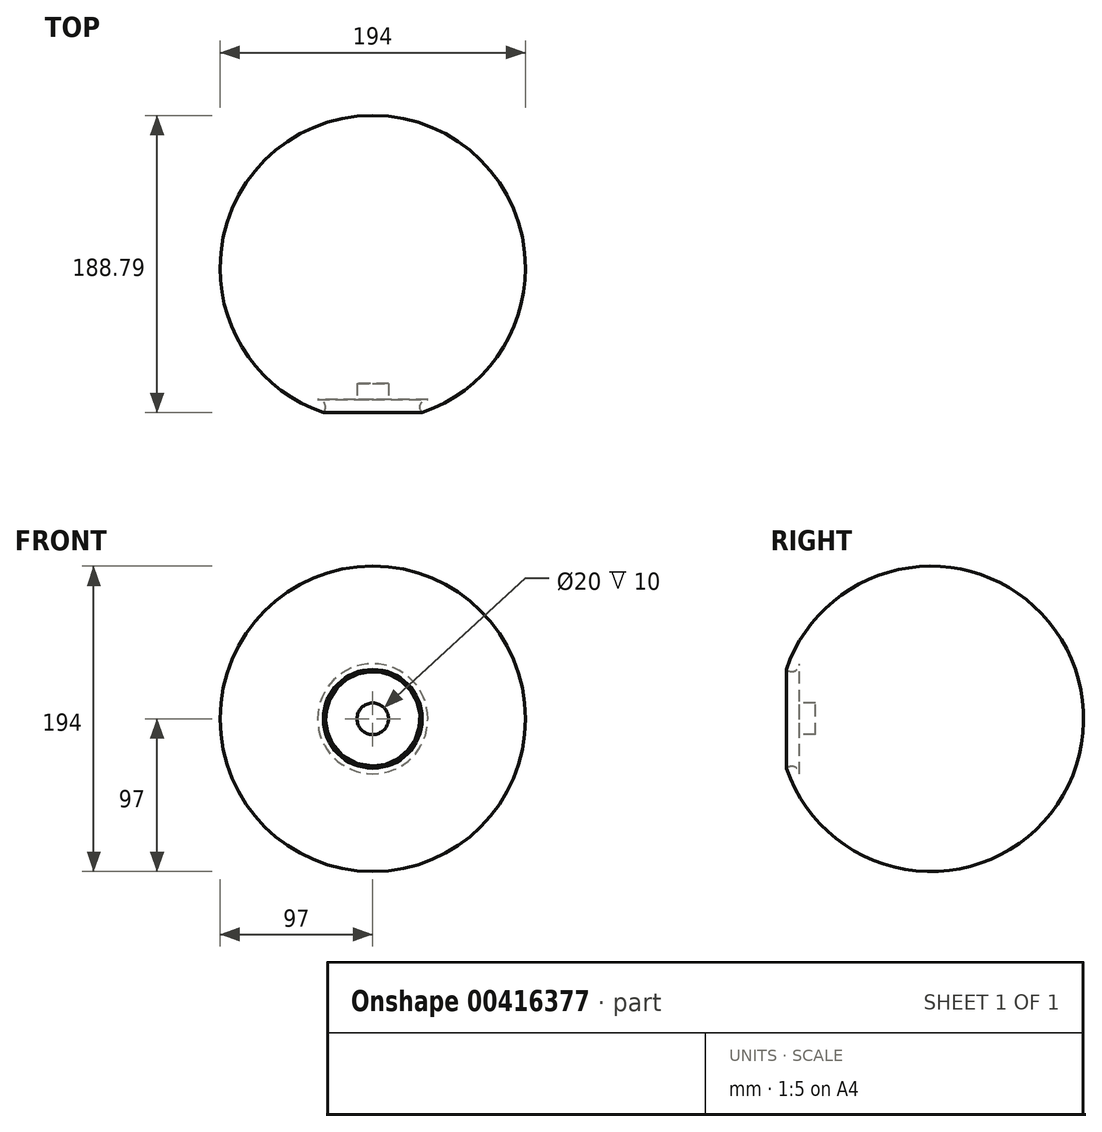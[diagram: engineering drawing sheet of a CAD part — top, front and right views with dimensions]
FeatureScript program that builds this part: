
annotation { "Feature Type Name" : "Feature", "Feature Type Description" : "" }
export const myFeature = defineFeature(function(context is Context, id is Id, definition is map)
    precondition{}
    {
        {
            var Q0;
            Q0=qCreatedBy(makeId("Front.planeOp"),FACE);
            var sketch = newSketch(context, id + "F0", { "sketchPlane" : qUnion([Q0])});
            skCircle(sketch, "E0", {"center": v(0, 0) * mm, "radius": 97 * mm});
            skCircle(sketch, "E1", {"center": v(-0.22, 0.55) * mm, "radius": 40 * mm});
            skLineSegment(sketch, "E2", {"start": v(0, 0) * mm, "end": v(97, 0) * mm});
            skLineSegment(sketch, "E3", {"start": v(0, 0) * mm, "end": v(-97, 0) * mm});
            skCircle(sketch, "E4", {"center": v(0, 0) * mm, "radius": 92 * mm});
            skSolve(sketch);
        }
        {
            var Q0;
            Q0=qCreatedBy(makeId("Right.planeOp"),FACE);
            var sketch = newSketch(context, id + "F1", { "sketchPlane" : qUnion([Q0])});
            skCircle(sketch, "E5", {"center": v(0, 0) * mm, "radius": 97 * mm});
            skLineSegment(sketch, "E6", {"start": v(0, 0) * mm, "end": v(-97, 0) * mm});
            skLineSegment(sketch, "E7", {"start": v(-88.37, 0) * mm, "end": v(-88.37, 40) * mm});
            skLineSegment(sketch, "E8", {"start": v(-88.37, 40) * mm, "end": v(-88.37, 35) * mm});
            skCircle(sketch, "E9", {"center": v(-88.37, 35) * mm, "radius": 5 * mm});
            skLineSegment(sketch, "E10", {"start": v(-83.37, 35) * mm, "end": v(-83.37, 10) * mm});
            skLineSegment(sketch, "E11", {"start": v(-83.37, 10) * mm, "end": v(-83.37, 0) * mm});
            skLineSegment(sketch, "E12", {"start": v(-83.37, 10) * mm, "end": v(-73.37, 10) * mm});
            skLineSegment(sketch, "E13", {"start": v(-73.37, 10) * mm, "end": v(-73.37, 0) * mm});
            skSolve(sketch);
        }
        {
            var Q0;
            {var subQ0=sQuery(id+"F0.wireOp",EDGE,"E2");var subQ1=sQuery(id+"F0.wireOp",EDGE,"E0");var subQ2=makeQuery(id+"F0.imprint","INTERSECT",VERTEX,{"derivedFrom":[subQ1,subQ0]});Q0=makeQuery(id+"F0.imprint","IMPRINT",FACE,{"disambiguationData":[TD([[makeQuery(id+"F0.imprint","IMPRINT",EDGE,{"disambiguationData":[TD([[subQ2,-1.0]])],"derivedFrom":subQ1}),1.0]])]});}
            var Q1;
            {var subQ0=sQuery(id+"F0.wireOp",EDGE,"E2");var subQ1=sQuery(id+"F0.wireOp",EDGE,"E1");var subQ2=makeQuery(id+"F0.imprint","INTERSECT",VERTEX,{"derivedFrom":[subQ1,subQ0]});Q1=makeQuery(id+"F0.imprint","IMPRINT",FACE,{"disambiguationData":[TD([[makeQuery(id+"F0.imprint","IMPRINT",EDGE,{"disambiguationData":[TD([[subQ2,-1.0]])],"derivedFrom":subQ1}),1.0]])]});}
            var Q2;
            {var subQ0=sQuery(id+"F0.wireOp",EDGE,"E2");var subQ1=sQuery(id+"F0.wireOp",EDGE,"E1");var subQ2=makeQuery(id+"F0.imprint","INTERSECT",VERTEX,{"derivedFrom":[subQ1,subQ0]});Q2=makeQuery(id+"F0.imprint","IMPRINT",FACE,{"disambiguationData":[TD([[makeQuery(id+"F0.imprint","IMPRINT",EDGE,{"disambiguationData":[TD([[subQ2,-1.0]])],"derivedFrom":subQ1}),-1.0]])]});}
            var Q3;
            Q3=sQuery(id+"F0.wireOp",EDGE,"E3");
            revolve(context, id + "F2", {"entities" : qUnion([Q0, Q1, Q2]), "axis" : qUnion([Q3]), "revolveType" : RevolveType.FULL});
        }
        {
            var Q0;
            {var subQ0=sQuery(id+"F1.wireOp",EDGE,"E8");Q0=makeQuery(id+"F1.imprint","IMPRINT",FACE,{"disambiguationData":[TD([[makeQuery(id+"F1.imprint","IMPRINT",EDGE,{"derivedFrom":subQ0}),1.0]])]});}
            var Q1;
            {var subQ1=sQuery(id+"F1.wireOp",EDGE,"E8");Q1=makeQuery(id+"F1.imprint","IMPRINT",FACE,{"disambiguationData":[TD([[makeQuery(id+"F1.imprint","IMPRINT",EDGE,{"derivedFrom":subQ1}),-1.0]])]});}
            var Q2;
            {var subQ0=sQuery(id+"F1.wireOp",EDGE,"E6");var subQ1=sQuery(id+"F1.wireOp",EDGE,"E5");var subQ2=makeQuery(id+"F1.imprint","INTERSECT",VERTEX,{"derivedFrom":[subQ1,subQ0]});Q2=makeQuery(id+"F1.imprint","IMPRINT",FACE,{"disambiguationData":[TD([[makeQuery(id+"F1.imprint","IMPRINT",EDGE,{"disambiguationData":[TD([[subQ2,1.0]])],"derivedFrom":subQ1}),1.0]])]});}
            var Q3;
            {var subQ0=sQuery(id+"F1.wireOp",EDGE,"E10");Q3=makeQuery(id+"F1.imprint","IMPRINT",FACE,{"disambiguationData":[TD([[makeQuery(id+"F1.imprint","IMPRINT",EDGE,{"derivedFrom":subQ0}),-1.0]])]});}
            var Q4;
            {var subQ0=sQuery(id+"F1.wireOp",EDGE,"E11");Q4=makeQuery(id+"F1.imprint","IMPRINT",FACE,{"disambiguationData":[TD([[makeQuery(id+"F1.imprint","IMPRINT",EDGE,{"derivedFrom":subQ0}),1.0]])]});}
            var Q5;
            Q5=sQuery(id+"F1.wireOp",EDGE,"E6");
            revolve(context, id + "F3", {"operationType" : NewBodyOperationType.REMOVE, "entities" : qUnion([Q0, Q1, Q2, Q3, Q4]), "axis" : qUnion([Q5]), "revolveType" : RevolveType.FULL, "oppositeDirection" : true});
        }
    });
